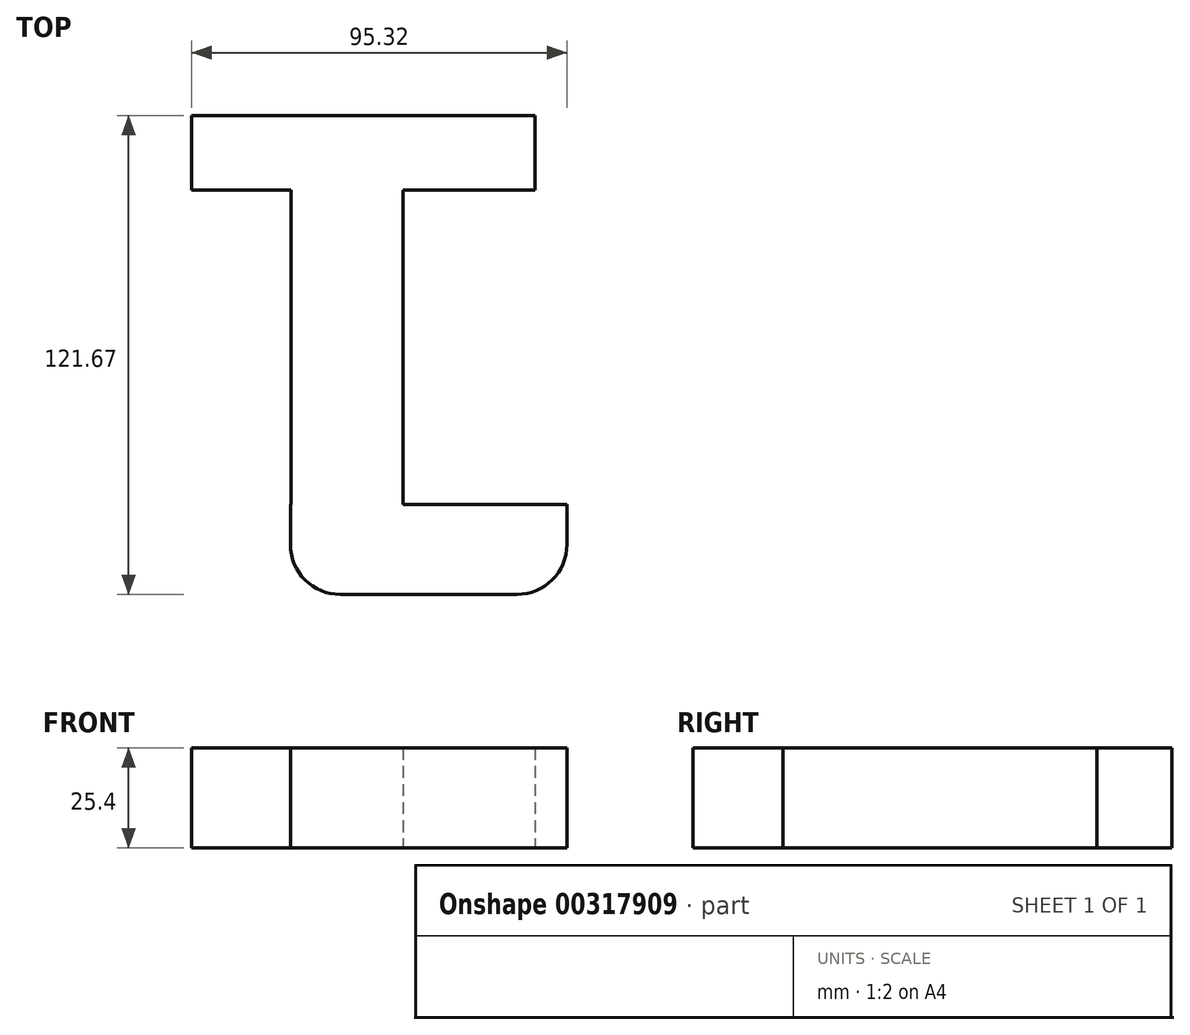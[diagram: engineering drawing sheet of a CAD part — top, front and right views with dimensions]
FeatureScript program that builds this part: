
annotation { "Feature Type Name" : "Feature", "Feature Type Description" : "" }
export const myFeature = defineFeature(function(context is Context, id is Id, definition is map)
    precondition{}
    {
        {
            var Q0;
            Q0=qCreatedBy(makeId("Top.planeOp"),FACE);
            var sketch = newSketch(context, id + "F0", { "sketchPlane" : qUnion([Q0])});
            skLineSegment(sketch, "E0.bottom", {"start": v(-14.38, 47.2) * mm, "end": v(14.01, 47.2) * mm});
            skLineSegment(sketch, "E0.top", {"start": v(-14.38, -32.63) * mm, "end": v(14.01, -32.63) * mm});
            skLineSegment(sketch, "E0.left", {"start": v(-14.38, 47.2) * mm, "end": v(-14.38, -32.63) * mm});
            skLineSegment(sketch, "E0.right", {"start": v(14.01, 47.2) * mm, "end": v(14.01, -32.63) * mm});
            skLineSegment(sketch, "E1.bottom", {"start": v(14.01, -32.63) * mm, "end": v(55.68, -32.63) * mm});
            skLineSegment(sketch, "E1.top", {"start": v(14.01, -55.5) * mm, "end": v(42.98, -55.5) * mm});
            skLineSegment(sketch, "E1.left", {"start": v(14.01, -32.63) * mm, "end": v(14.01, -55.5) * mm});
            skLineSegment(sketch, "E1.right", {"start": v(55.68, -32.63) * mm, "end": v(55.68, -42.8) * mm});
            skLineSegment(sketch, "E2.bottom", {"start": v(-39.64, 66.18) * mm, "end": v(47.56, 66.18) * mm});
            skLineSegment(sketch, "E2.top", {"start": v(-39.64, 47.2) * mm, "end": v(47.56, 47.2) * mm});
            skLineSegment(sketch, "E2.left", {"start": v(-39.64, 66.18) * mm, "end": v(-39.64, 47.2) * mm});
            skLineSegment(sketch, "E2.right", {"start": v(47.56, 66.18) * mm, "end": v(47.56, 47.2) * mm});
            skPoint(sketch, "E3.visualSharp", {"position": v(55.68, -55.5) * mm});
            skArc(sketch, "E3.filletArc", {"start": v(42.98, -55.5) * mm, "mid": v(51.96, -51.77) * mm, "end": v(55.68, -42.8) * mm});
            skLineSegment(sketch, "E4.bottom", {"start": v(14.01, -32.63) * mm, "end": v(-14.56, -32.63) * mm});
            skLineSegment(sketch, "E4.top", {"start": v(14.01, -55.5) * mm, "end": v(-1.86, -55.5) * mm});
            skLineSegment(sketch, "E4.right", {"start": v(-14.56, -32.63) * mm, "end": v(-14.56, -42.8) * mm});
            skPoint(sketch, "E5.visualSharp", {"position": v(-14.56, -55.5) * mm});
            skArc(sketch, "E5.filletArc", {"start": v(-14.56, -42.8) * mm, "mid": v(-10.84, -51.77) * mm, "end": v(-1.86, -55.5) * mm});
            skLineSegment(sketch, "E6.bottom", {"start": v(55.68, -32.63) * mm, "end": v(33.92, -32.63) * mm});
            skLineSegment(sketch, "E6.top", {"start": v(55.68, -14.56) * mm, "end": v(33.92, -14.56) * mm});
            skLineSegment(sketch, "E6.left", {"start": v(55.68, -32.63) * mm, "end": v(55.68, -14.56) * mm});
            skLineSegment(sketch, "E6.right", {"start": v(33.92, -32.63) * mm, "end": v(33.92, -14.56) * mm});
            skSolve(sketch);
        }
        {
            var Q0;
            Q0=makeQuery(id+"F0.imprint","IMPRINT",FACE,{"disambiguationData":[TD([[makeQuery(id+"F0.imprint","IMPRINT",EDGE,{"derivedFrom":sQuery(id+"F0.wireOp",EDGE,"E2.bottom")}),-1.0]])]});
            var Q1;
            {var subQ0=sQuery(id+"F0.wireOp",EDGE,"E0.left");Q1=makeQuery(id+"F0.imprint","IMPRINT",FACE,{"disambiguationData":[TD([[makeQuery(id+"F0.imprint","IMPRINT",EDGE,{"derivedFrom":subQ0}),1.0]])]});}
            var Q2;
            Q2=makeQuery(id+"F0.imprint","IMPRINT",FACE,{"disambiguationData":[TD([[makeQuery(id+"F0.imprint","IMPRINT",EDGE,{"derivedFrom":sQuery(id+"F0.wireOp",EDGE,"E4.top")}),-1.0]])]});
            var Q3;
            Q3=makeQuery(id+"F0.imprint","IMPRINT",FACE,{"disambiguationData":[TD([[makeQuery(id+"F0.imprint","IMPRINT",EDGE,{"derivedFrom":sQuery(id+"F0.wireOp",EDGE,"E1.bottom")}),-1.0]])]});
            var Q4;
            Q4=makeQuery(id+"F0.imprint","IMPRINT",FACE,{"disambiguationData":[TD([[makeQuery(id+"F0.imprint","IMPRINT",EDGE,{"derivedFrom":sQuery(id+"F0.wireOp",EDGE,"E6.bottom")}),-1.0]])]});
            extrude(context, id + "F1", {"entities" : qUnion([Q0, Q1, Q2, Q3, Q4]), "depth" : 25.4 * mm});
        }
    });
